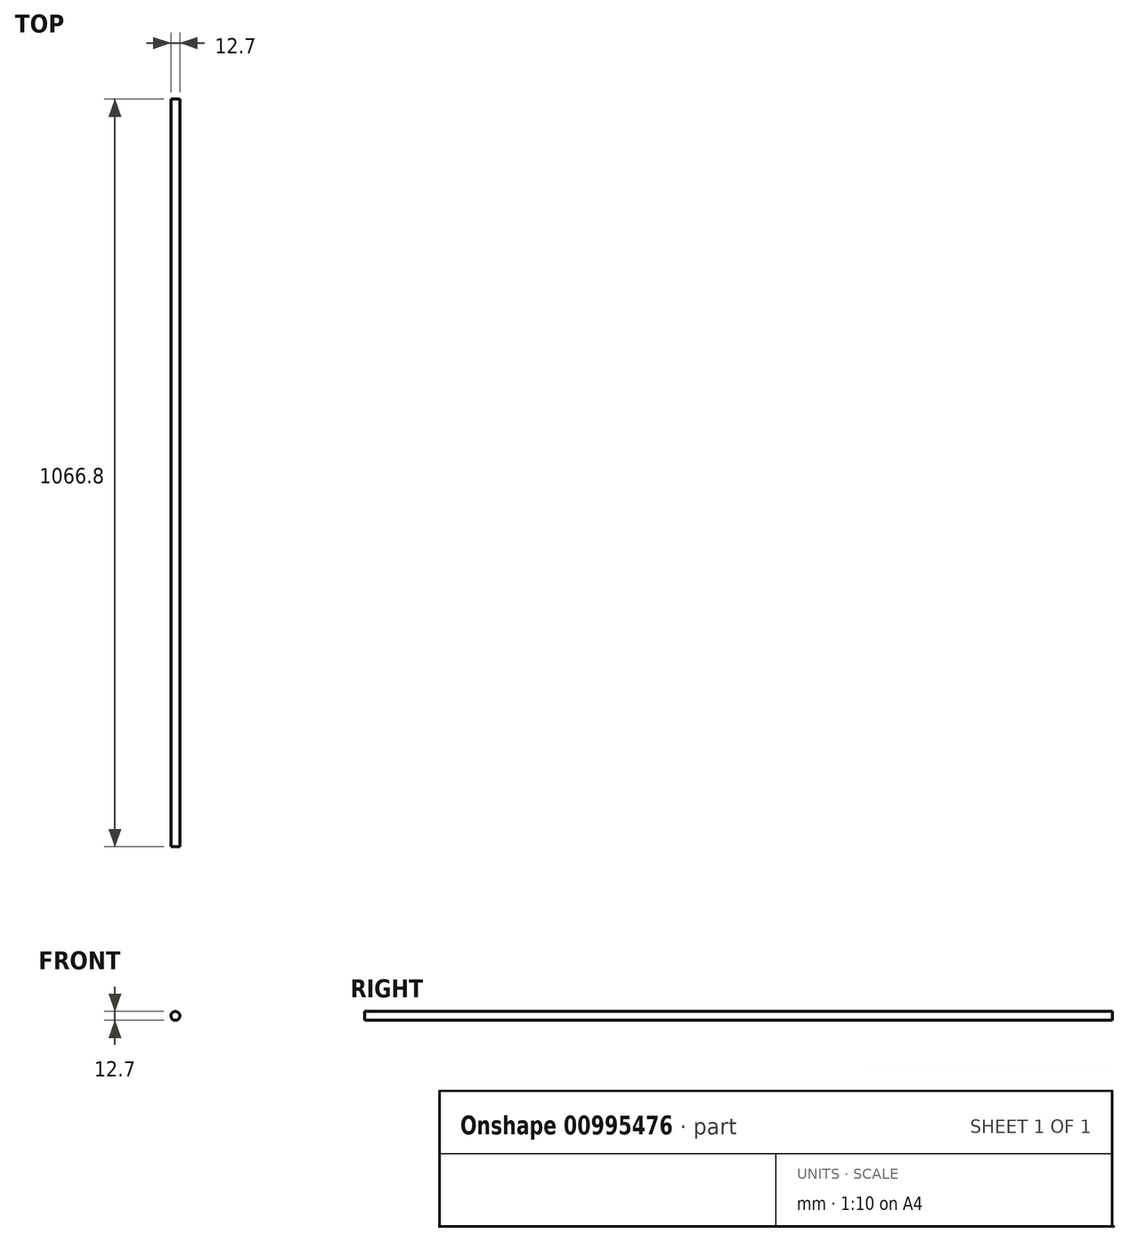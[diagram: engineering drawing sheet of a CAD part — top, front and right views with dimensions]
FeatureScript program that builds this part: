
annotation { "Feature Type Name" : "Feature", "Feature Type Description" : "" }
export const myFeature = defineFeature(function(context is Context, id is Id, definition is map)
    precondition{}
    {
        {
            var Q0;
            Q0=qCreatedBy(makeId("Front.planeOp"),FACE);
            var sketch = newSketch(context, id + "F0", { "sketchPlane" : qUnion([Q0])});
            skCircle(sketch, "E0", {"center": v(0, 0) * mm, "radius": 6.35 * mm});
            skSolve(sketch);
        }
        {
            var Q0;
            Q0 = qSketchRegion(id + "F0", true);
            extrude(context, id + "F1", {"entities" : qUnion([Q0]), "depth" : 1066.8 * mm, "offsetDistance" : 25.4 * mm});
        }
    });
